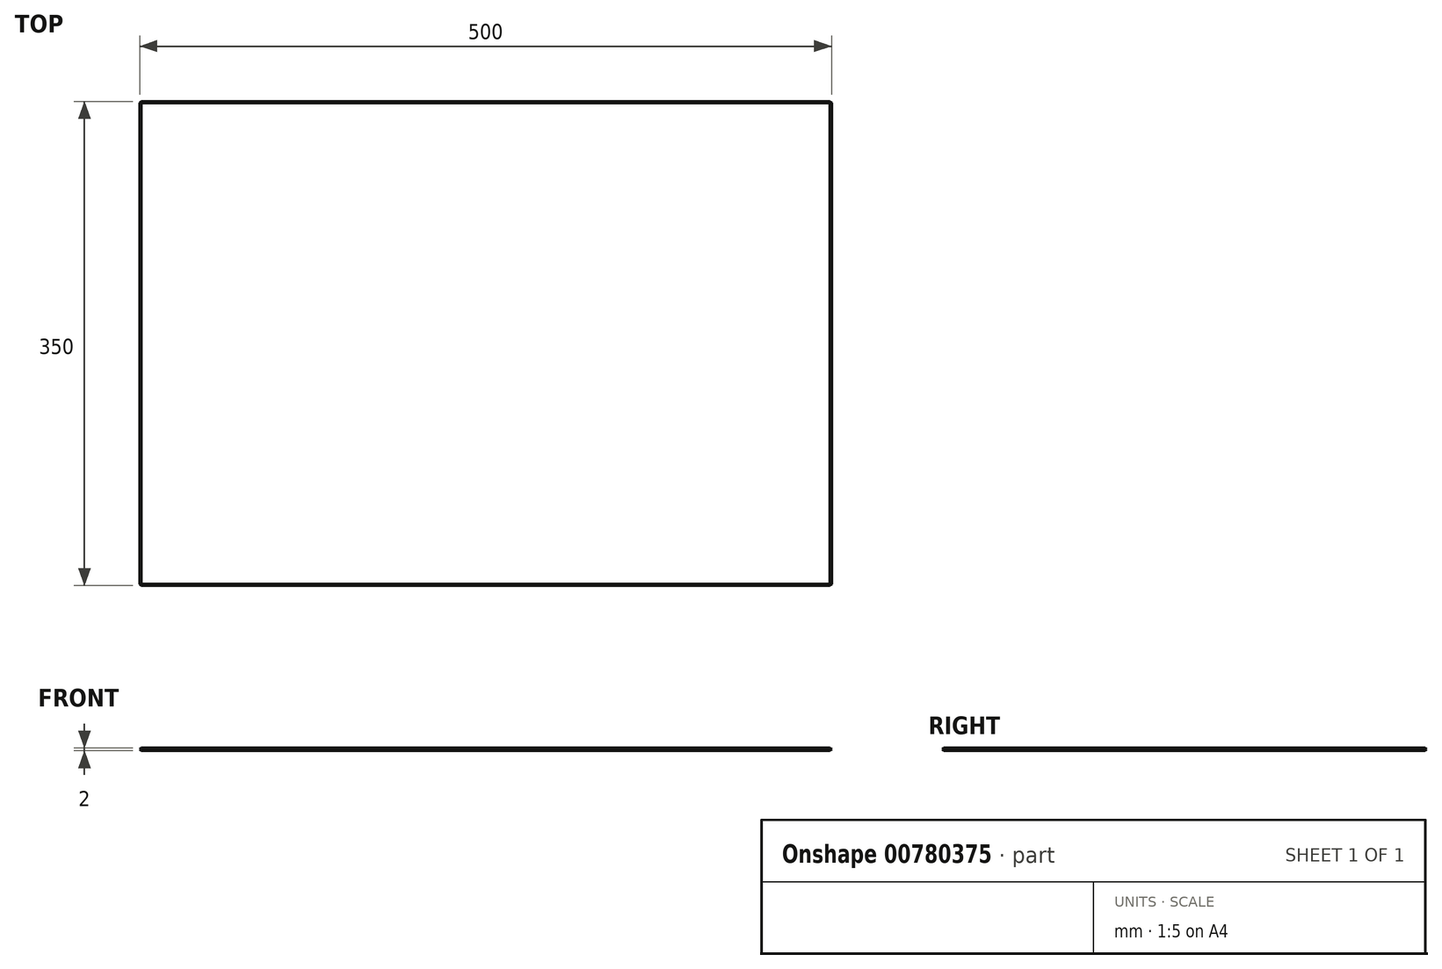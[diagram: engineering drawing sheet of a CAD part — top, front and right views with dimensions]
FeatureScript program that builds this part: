
annotation { "Feature Type Name" : "Feature", "Feature Type Description" : "" }
export const myFeature = defineFeature(function(context is Context, id is Id, definition is map)
    precondition{}
    {
        {
            var Q0;
            Q0=qCreatedBy(makeId("Top.planeOp"),FACE);
            var sketch = newSketch(context, id + "F0", { "sketchPlane" : qUnion([Q0])});
            skLineSegment(sketch, "E0.bottom", {"start": v(250, -175) * mm, "end": v(-250, -175) * mm});
            skLineSegment(sketch, "E0.top", {"start": v(250, 175) * mm, "end": v(-250, 175) * mm});
            skLineSegment(sketch, "E0.left", {"start": v(250, -175) * mm, "end": v(250, 175) * mm});
            skLineSegment(sketch, "E0.right", {"start": v(-250, -175) * mm, "end": v(-250, 175) * mm});
            skPoint(sketch, "E0.middle", {"position": v(0, 0) * mm});
            skSolve(sketch);
        }
        {
            var Q0;
            Q0=makeQuery(id+"F0.imprint","IMPRINT",FACE,{"disambiguationData":[TD([[makeQuery(id+"F0.imprint","IMPRINT",EDGE,{"derivedFrom":sQuery(id+"F0.wireOp",EDGE,"E0.bottom")}),-1.0]])]});
            extrude(context, id + "F1", {"entities" : qUnion([Q0]), "depth" : 2 * mm, "offsetDistance" : 25 * mm});
        }
        {
            var Q0;
            Q0=makeQuery(id+"F1.opExtrude","CAP_EDGE",EDGE,{"disambiguationData":[OSD([sQuery(id+"F0.wireOp",EDGE,"E0.top")])],"isStart":true});
            var Q1;
            Q1=makeQuery(id+"F1.opExtrude","CAP_EDGE",EDGE,{"disambiguationData":[OSD([sQuery(id+"F0.wireOp",EDGE,"E0.right")])],"isStart":true});
            var Q2;
            Q2=makeQuery(id+"F1.opExtrude","CAP_EDGE",EDGE,{"disambiguationData":[OSD([sQuery(id+"F0.wireOp",EDGE,"E0.right")])],"isStart":false});
            var Q3;
            Q3=makeQuery(id+"F1.opExtrude","CAP_EDGE",EDGE,{"disambiguationData":[OSD([sQuery(id+"F0.wireOp",EDGE,"E0.top")])],"isStart":false});
            var Q4;
            Q4=makeQuery(id+"F1.opExtrude","CAP_EDGE",EDGE,{"disambiguationData":[OSD([sQuery(id+"F0.wireOp",EDGE,"E0.left")])],"isStart":true});
            var Q5;
            Q5=makeQuery(id+"F1.opExtrude","CAP_FACE",FACE,{"disambiguationData":[OSD([sQuery(id+"F0.wireOp",EDGE,"E0.bottom"),sQuery(id+"F0.wireOp",EDGE,"E0.top"),sQuery(id+"F0.wireOp",EDGE,"E0.left"),sQuery(id+"F0.wireOp",EDGE,"E0.right")])],"isStart":false});
            var Q6;
            Q6=makeQuery(id+"F1.opExtrude","CAP_FACE",FACE,{"disambiguationData":[OSD([sQuery(id+"F0.wireOp",EDGE,"E0.bottom"),sQuery(id+"F0.wireOp",EDGE,"E0.top"),sQuery(id+"F0.wireOp",EDGE,"E0.left"),sQuery(id+"F0.wireOp",EDGE,"E0.right")])],"isStart":true});
            var Q7;
            Q7=makeQuery(id+"F1.opExtrude","SWEPT_EDGE",EDGE,{"disambiguationData":[OSD([sQuery(id+"F0.wireOp",EDGE,"E0.bottom"),sQuery(id+"F0.wireOp",EDGE,"E0.right")])]});
            var Q8;
            Q8=makeQuery(id+"F1.opExtrude","SWEPT_EDGE",EDGE,{"disambiguationData":[OSD([sQuery(id+"F0.wireOp",EDGE,"E0.top"),sQuery(id+"F0.wireOp",EDGE,"E0.right")])]});
            var Q9;
            Q9=makeQuery(id+"F1.opExtrude","SWEPT_EDGE",EDGE,{"disambiguationData":[OSD([sQuery(id+"F0.wireOp",EDGE,"E0.top"),sQuery(id+"F0.wireOp",EDGE,"E0.left")])]});
            var Q10;
            Q10=makeQuery(id+"F1.opExtrude","SWEPT_EDGE",EDGE,{"disambiguationData":[OSD([sQuery(id+"F0.wireOp",EDGE,"E0.bottom"),sQuery(id+"F0.wireOp",EDGE,"E0.left")])]});
            chamfer(context, id + "F2", {"entities" : qUnion([Q0, Q1, Q2, Q3, Q4, Q5, Q6, Q7, Q8, Q9, Q10]), "width" : 1 * mm, "tangentPropagation" : true});
        }
    });
